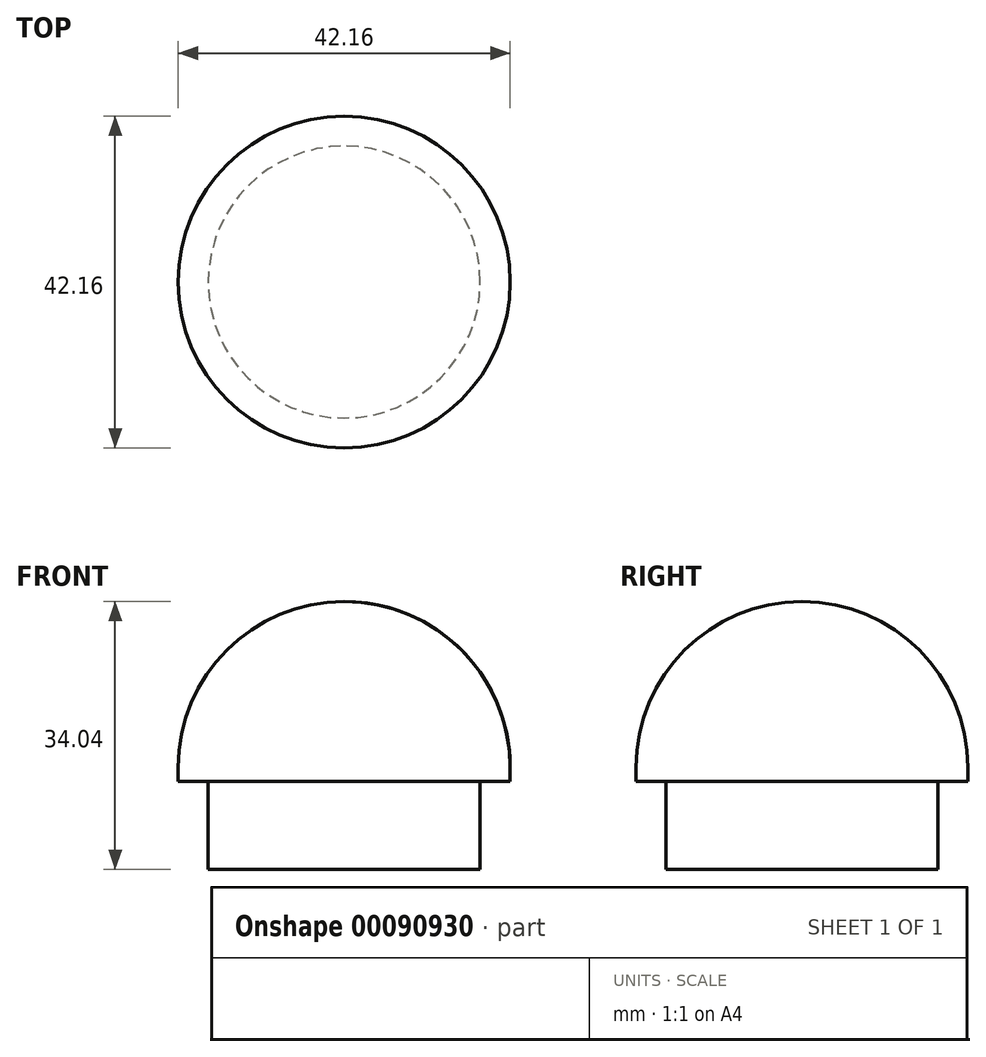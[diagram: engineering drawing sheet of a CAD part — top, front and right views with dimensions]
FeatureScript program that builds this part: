
annotation { "Feature Type Name" : "Feature", "Feature Type Description" : "" }
export const myFeature = defineFeature(function(context is Context, id is Id, definition is map)
    precondition{}
    {
        {
            var Q0;
            Q0=qCreatedBy(makeId("Front.planeOp"),FACE);
            var sketch = newSketch(context, id + "F0", { "sketchPlane" : qUnion([Q0])});
            skLineSegment(sketch, "E0", {"start": v(-17.27, 0) * mm, "end": v(-17.27, 11.18) * mm});
            skLineSegment(sketch, "E1", {"start": v(-17.27, 11.18) * mm, "end": v(-21.08, 11.18) * mm});
            skLineSegment(sketch, "E2", {"start": v(-21.08, 11.18) * mm, "end": v(-21.08, 12.95) * mm});
            skArc(sketch, "E3", {"start": v(0, 34.04) * mm, "mid": v(-14.9, 27.86) * mm, "end": v(-21.08, 12.95) * mm});
            skLineSegment(sketch, "E4", {"start": v(-17.27, 0) * mm, "end": v(0, 0) * mm});
            skLineSegment(sketch, "E5", {"start": v(0, 34.04) * mm, "end": v(0, 0) * mm});
            skSolve(sketch);
        }
        {
            var Q0;
            Q0 = qSketchRegion(id + "F0", true);
            var Q1;
            Q1=sQuery(id+"F0.wireOp",EDGE,"E5");
            revolve(context, id + "F1", {"entities" : qUnion([Q0]), "axis" : qUnion([Q1]), "revolveType" : RevolveType.FULL});
        }
    });
